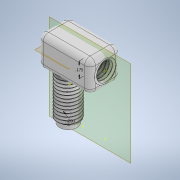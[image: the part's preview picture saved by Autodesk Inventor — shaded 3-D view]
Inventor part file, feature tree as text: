
AUTODESK INVENTOR PART (.ipt)
format: ipt  version: 2020 (Build 240168000, 168)  size: 1,738,240 bytes
history: native  units: in
note: dims shown in document units (in); Inventor stores cm internally (conversion verified against a paired STEP export)
features: sketch x12, extrude x4, hole x3, revolve x3, thread x2, plane x2, helix x2, fillet x1
ambient origin geometry x8: Origin, YZ Plane, XZ Plane, XY Plane, X Axis, Y Axis, Z Axis, Center Point
bodies: Solid1 (feature_tree), Solid2 (feature_tree), Solid3 (feature_tree)
feature tree (29):
  extrude  "Extrusion1"  Depth=0.25in TaperAngle=0.0deg
  thread  "Thread1"  [1 undecoded]
  sketch  "Sketch2"  dims[d5=0.2in d13=0.05in d14=0.0in]
  extrude  "Extrusion2"  Depth=0.05in TaperAngle=0.0deg
  extrude  "Extrusion3"  Depth=0.25in
  sketch  "Sketch6"  dims[d26=0.175in d27=0.25in d28=0.0in]
  plane  "Work Plane1"
  hole  "Hole2"  [1 undecoded]
  extrude  "Extrusion4"  Depth=0.25in TaperAngle=0.0deg
  sketch  "Sketch8"  dims[d38=0.04in d39=0.75in d40=0.332in d41=0.25in d42=0.5635in d43=0.445in d44=135.0deg d45=0.0625in]
  hole  "Hole3"  [1 undecoded]
  thread  "Thread2"  [1 undecoded]
  hole  "Hole4"  [1 undecoded]
  plane  "Work Plane2"
  fillet  "Fillet1"  Radius=0.3779in
  revolve  "Revolution1"  [1 undecoded]
  helix  "Coil1"  [1 undecoded]
  revolve  "Revolution2"  [1 undecoded]
  revolve  "Revolution3"  [1 undecoded]
  helix  "Coil2"  [1 undecoded]
  sketch  "Sketch1"  dims[d0=0.25in d1=0.5in d2=0.0in d3=0.5in d4=0.0in]
  sketch  "Sketch3"  dims[d16=0.75in d17=0.332in d18=0.25in d19=0.5635in d20=1.378in d21=135.0deg d22=0.35in]
  sketch  "Sketch4"  dims[d23=0.35in d24=0.35in d25=0.0in]
  sketch  "Sketch7"  dims[d29=0.25in d30=0.75in d31=0.332in d32=0.25in d33=0.5635in d34=0.25in d35=0.0in d36=0.5in d37=0.0in]
  sketch  "Sketch9"  dims[d46=0.3779in d47=0.0057in d48=0.0057in d51=0.0357in d53=0.3779in]
  sketch  "Sketch10"  dims[d55=0.0in]
  sketch  "Sketch11"  dims[d56=0.0358in d57=0.3214in d58=0.3937in d59=0.0in d60=0.0in d61=0.0in d62=0.0in d63=0.0in d64=0.3779in d65=0.0057in d66=0.0057in d69=0.0357in]
  sketch  "Sketch12"  dims[d71=0.3779in d73=0.0in]
  sketch  "Sketch13"  dims[d74=0.0in d75=0.0358in d76=0.5714in d77=0.3937in d78=0.0in d79=0.0in d80=0.0in d81=0.0in d82=0.0in]
note: 10 required parameter values undecoded (feature->parameter linkage not recoverable at this tier; creation-order binding heuristic only, values carry confidence <= 0.55)